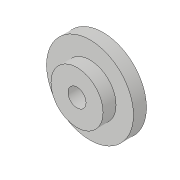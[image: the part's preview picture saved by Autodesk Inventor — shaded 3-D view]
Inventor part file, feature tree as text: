
AUTODESK INVENTOR PART (.ipt)
format: ipt  version: 2018.3 (Build 223284000, 284)  size: 92,672 bytes
history: native  units: in
note: dims shown in document units (in); Inventor stores cm internally (conversion verified against a paired STEP export)
features: extrude x2, sketch x2
ambient origin geometry x8: Origin, YZ Plane, XZ Plane, XY Plane, X Axis, Y Axis, Z Axis, Center Point
bodies: Body1 (feature_tree)
feature tree (4):
  extrude  "Extrusion4"  Depth=0.1867in TaperAngle=0.0deg
  extrude  "Extrusion5"  Depth=0.0933in TaperAngle=0.0deg
  sketch  "Sketch4"  dims[d9=0.13in d11=0.1867in d12=0.0in]
  sketch  "Sketch5"  dims[d13=0.125in d14=0.0933in d15=0.0in d16=0.374in]
